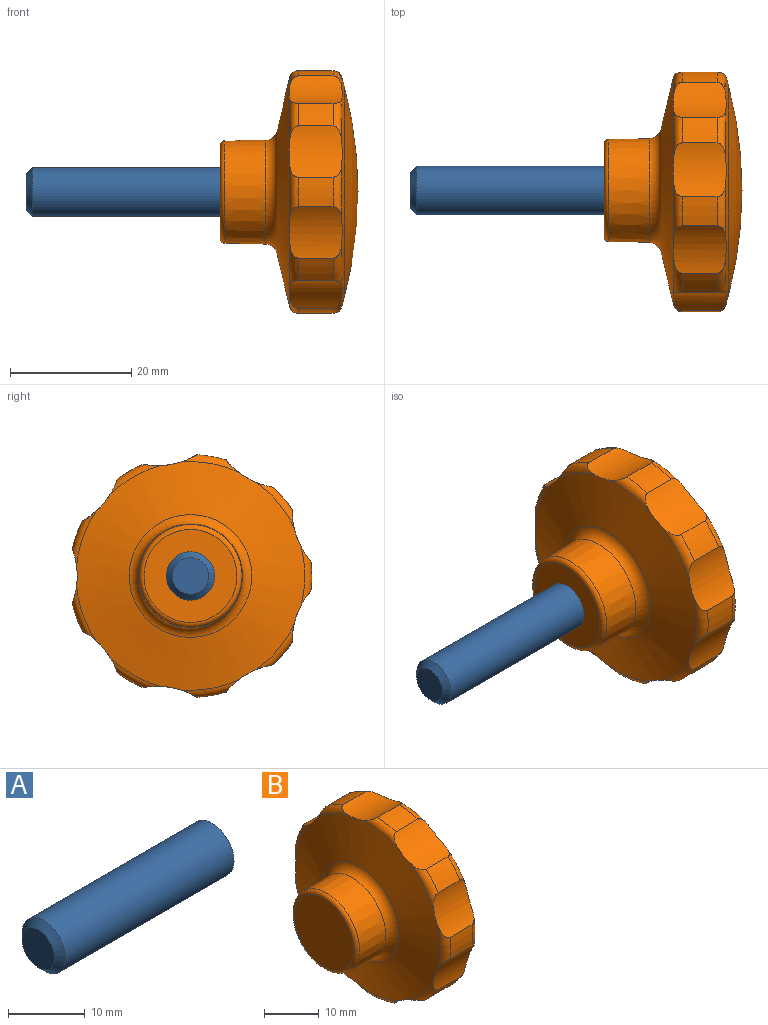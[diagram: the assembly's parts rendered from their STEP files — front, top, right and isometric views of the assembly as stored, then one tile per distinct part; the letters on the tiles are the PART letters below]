
ASSEMBLY  parts=2 mates=1
PART A: 4 faces, bbox 32x8x8 mm
  f0: cylinder r=4mm len=31mm, axis (-1,0,0), area 779.1mm2, adj f1,f3
  f1: cone r=3mm half-angle=45deg, axis (1,0,0), area 31.1mm2, adj f0,f2
  f2: plane 6x6mm, normal (-1,0,0), area 28.3mm2, adj f1
  f3: plane 8x8mm, normal (1,0,0), area 50.3mm2, adj f0
PART B: 45 faces, bbox 22.7x43.2x43.3 mm
  f0: cylinder r=20mm len=5.7mm, axis (-1,0,0), area 27.8mm2, adj f9,f16,f43,f44
  f1: cylinder r=20mm len=5.7mm, axis (-1,0,0), area 27.8mm2, adj f10,f17,f42,f43
  f2: cylinder r=20mm len=5.7mm, axis (-1,0,0), area 27.8mm2, adj f11,f18,f41,f42
  f3: cylinder r=20mm len=5.7mm, axis (-1,0,0), area 27.8mm2, adj f12,f19,f40,f41
  f4: cylinder r=20mm len=5.7mm, axis (-1,0,0), area 27.8mm2, adj f13,f20,f39,f40
  f5: cylinder r=20mm len=5.7mm, axis (-1,0,0), area 27.8mm2, adj f14,f21,f38,f39
  f6: cylinder r=20mm len=5.7mm, axis (-1,0,0), area 27.8mm2, adj f15,f22,f37,f38
  f7: cylinder r=20mm len=5.7mm, axis (-1,0,0), area 27.8mm2, adj f23,f32,f36,f37
  f8: torus R=18.5mm, axis (-1,0,0), area 11.9mm2, adj f28,f29,f36,f44
  f9: torus R=18.5mm, axis (-1,0,0), area 11.9mm2, adj f0,f28,f43,f44
  f10: torus R=18.5mm, axis (-1,0,0), area 11.9mm2, adj f1,f28,f42,f43
  f11: torus R=18.5mm, axis (-1,0,0), area 11.9mm2, adj f2,f28,f41,f42
  f12: torus R=18.5mm, axis (-1,0,0), area 11.9mm2, adj f3,f28,f40,f41
  f13: torus R=18.5mm, axis (-1,0,0), area 11.9mm2, adj f4,f28,f39,f40
  f14: torus R=18.5mm, axis (-1,0,0), area 11.9mm2, adj f5,f28,f38,f39
  f15: torus R=18.5mm, axis (-1,0,0), area 11.9mm2, adj f6,f28,f37,f38
  f16: torus R=18.5mm, axis (1,0,0), area 12.6mm2, adj f0,f30,f43,f44
  f17: torus R=18.5mm, axis (1,0,0), area 12.6mm2, adj f1,f30,f42,f43
  f18: torus R=18.5mm, axis (1,0,0), area 12.6mm2, adj f2,f30,f41,f42
  f19: torus R=18.5mm, axis (1,0,0), area 12.6mm2, adj f3,f30,f40,f41
  f20: torus R=18.5mm, axis (1,0,0), area 12.6mm2, adj f4,f30,f39,f40
  f21: torus R=18.5mm, axis (1,0,0), area 12.6mm2, adj f5,f30,f38,f39
  f22: torus R=18.5mm, axis (1,0,0), area 12.6mm2, adj f6,f30,f37,f38
  f23: torus R=18.5mm, axis (1,0,0), area 12.6mm2, adj f7,f30,f36,f37
  f24: plane 15.33x15.33mm, normal (-1,0,0), area 184.5mm2, adj f35
  f25: sphere r=68.17mm, area 971.7mm2, adj f26
  f26: cone r=17.5mm half-angle=15deg, axis (-1,0,0), area 25.3mm2, adj f25,f27
  f27: cone r=17.66mm half-angle=45deg, axis (1,0,0), area 25.5mm2, adj f26,f28
  f28: sphere r=68.17mm, area 142.8mm2, adj f8,f9,f10,f11,f12,f13,f14,f15
  f29: cylinder r=20mm len=5.7mm, axis (-1,0,0), area 27.8mm2, adj f8,f33,f36,f44
  f30: cone r=8.6mm half-angle=76.7deg, axis (1,0,0), area 812.3mm2, adj f16,f17,f18,f19,f20,f21,f22,f23
  f31: cone r=8.45mm half-angle=1deg, axis (1,0,0), area 356.5mm2, adj f34,f35
  f32: torus R=18.5mm, axis (-1,0,0), area 11.9mm2, adj f7,f28,f36,f37
  f33: torus R=18.5mm, axis (1,0,0), area 12.6mm2, adj f29,f30,f36,f44
  f34: torus R=10.57mm, axis (-1,0,0), area 151.6mm2, adj f30,f31
  f35: torus R=7.66mm, axis (1,0,0), area 63.8mm2, adj f24,f31
  f36: cylinder r=12.5mm len=8.6mm, axis (1,0,0), area 75.7mm2, adj f7,f8,f23,f28,f29,f30,f32,f33
  f37: cylinder r=12.5mm len=9mm, axis (1,0,0), area 75.7mm2, adj f6,f7,f15,f22,f23,f28,f30,f32
  f38: cylinder r=12.5mm len=8.6mm, axis (1,0,0), area 75.7mm2, adj f5,f6,f14,f15,f21,f22,f28,f30
  f39: cylinder r=12.5mm len=8.86mm, axis (1,0,0), area 75.7mm2, adj f4,f5,f13,f14,f20,f21,f28,f30
  f40: cylinder r=12.5mm len=8.6mm, axis (1,0,0), area 75.7mm2, adj f3,f4,f12,f13,f19,f20,f28,f30
  f41: cylinder r=12.5mm len=8.6mm, axis (1,0,0), area 75.7mm2, adj f2,f3,f11,f12,f18,f19,f28,f30
  f42: cylinder r=12.5mm len=8.6mm, axis (1,0,0), area 75.7mm2, adj f1,f2,f10,f11,f17,f18,f28,f30
  f43: cylinder r=12.5mm len=8.6mm, axis (1,0,0), area 75.7mm2, adj f0,f1,f9,f10,f16,f17,f28,f30
  f44: cylinder r=12.5mm len=8.86mm, axis (1,0,0), area 75.7mm2, adj f0,f8,f9,f16,f28,f29,f30,f33
PLACE A at identity
PLACE B at identity
MATE fastened A.f0 <-> B.f0  axis (-1,0,0) through (-75.08,0,37.01)mm
